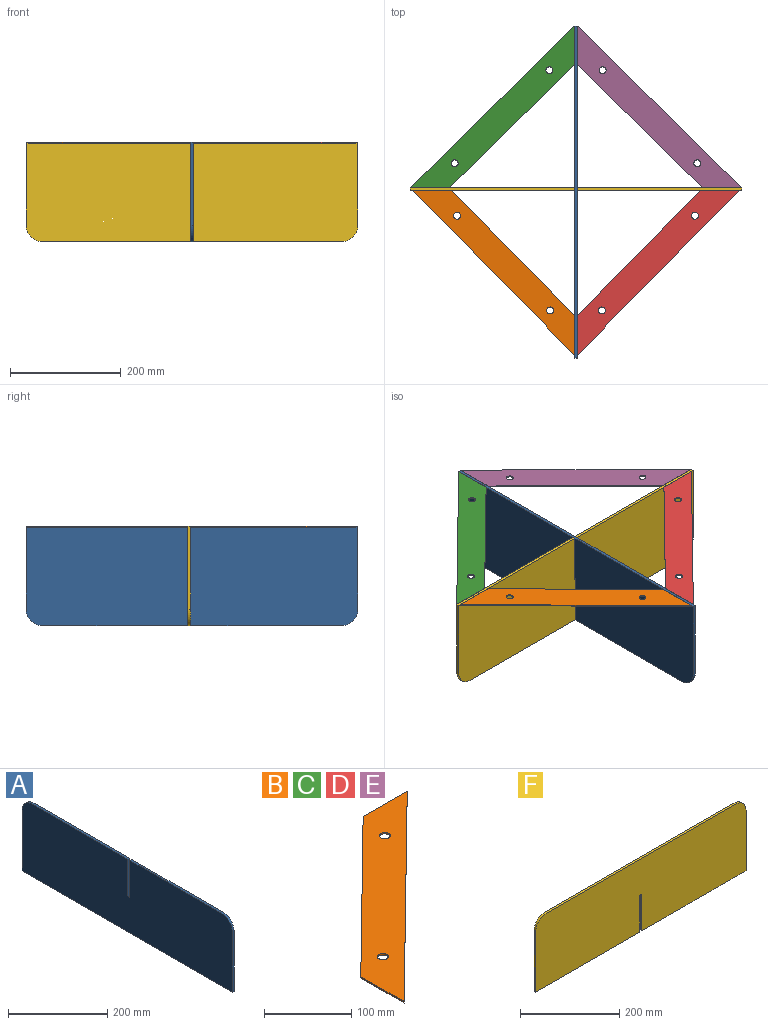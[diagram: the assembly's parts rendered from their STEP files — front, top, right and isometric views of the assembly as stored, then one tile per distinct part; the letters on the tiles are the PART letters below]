
ASSEMBLY  parts=6 mates=9
PART A: 12 faces, bbox 5x600x180 mm
  f0: plane 91x5mm, normal (0,1,0), area 455mm2, adj f1,f7,f8,f9
  f1: plane 262x5mm, normal (0,0,1), area 1310mm2, adj f0,f8,f9,f10
  f2: plane 150x5mm, normal (0,-1,0), area 750mm2, adj f3,f8,f9,f10
  f3: plane 600x5mm, normal (0,0,-1), area 3000mm2, adj f2,f4,f8,f9
  f4: plane 150x5mm, normal (0,1,0), area 750mm2, adj f3,f8,f9,f11
  f5: plane 272x5mm, normal (0,0,1), area 1360mm2, adj f6,f8,f9,f11
  f6: plane 91x5mm, normal (0,-1,0), area 455mm2, adj f5,f7,f8,f9
  f7: plane 6x5mm, normal (0,0,1), area 30mm2, adj f0,f6,f8,f9
  f8: plane 600x180mm, normal (1,0,0), area 107067.7mm2, adj f0,f1,f2,f3,f4,f5,f6,f7
  f9: plane 600x180mm, normal (-1,0,0), area 107067.7mm2, adj f0,f1,f2,f3,f4,f5,f6,f7
  f10: cylinder r=30mm len=30mm, axis (-1,0,0), area 235.6mm2, adj f1,f2,f8,f9
  f11: cylinder r=30mm len=30mm, axis (1,0,0), area 235.6mm2, adj f4,f5,f8,f9
PART B: 8 faces, bbox 297.5x292.5x2 mm
  f0: plane 70.12x2mm, normal (-1,0,0), area 140.2mm2, adj f1,f3,f4,f5
  f1: plane 226.18x222.38mm, normal (-0.7,0.71,0), area 634.4mm2, adj f0,f2,f4,f5
  f2: plane 71.32x2mm, normal (0,1,0), area 142.6mm2, adj f1,f3,f4,f5
  f3: plane 297.5x292.5mm, normal (0.7,-0.71,0), area 834.4mm2, adj f0,f2,f4,f5
  f4: plane 297.5x292.5mm, normal (0,0,1), area 18114.6mm2, adj f0,f1,f2,f3,f6,f7
  f5: plane 297.5x292.5mm, normal (0,0,-1), area 18114.6mm2, adj f0,f1,f2,f3,f6,f7
  f6: cylinder r=6.25mm len=12.5mm, axis (0,0,-1), area 78.5mm2, adj f4,f5
  f7: cylinder r=6.25mm len=12.5mm, axis (0,0,-1), area 78.5mm2, adj f4,f5
PART C: same geometry as B
PART D: same geometry as B
PART E: same geometry as B
PART F: 12 faces, bbox 600x5x180 mm
  f0: plane 91x5mm, normal (-1,0,0), area 455mm2, adj f1,f7,f8,f9
  f1: plane 297x5mm, normal (0,0,-1), area 1485mm2, adj f0,f2,f8,f9
  f2: plane 150x5mm, normal (1,0,0), area 750mm2, adj f1,f8,f9,f10
  f3: plane 540x5mm, normal (0,0,1), area 2700mm2, adj f8,f9,f10,f11
  f4: plane 150x5mm, normal (-1,0,0), area 750mm2, adj f5,f8,f9,f11
  f5: plane 297x5mm, normal (0,0,-1), area 1485mm2, adj f4,f6,f8,f9
  f6: plane 91x5mm, normal (1,0,0), area 455mm2, adj f5,f7,f8,f9
  f7: plane 6x5mm, normal (0,0,-1), area 30mm2, adj f0,f6,f8,f9
  f8: plane 600x180mm, normal (0,-1,0), area 107067.7mm2, adj f0,f1,f2,f3,f4,f5,f6,f7
  f9: plane 600x180mm, normal (0,1,0), area 107067.7mm2, adj f0,f1,f2,f3,f4,f5,f6,f7
  f10: cylinder r=30mm len=30mm, axis (0,-1,0), area 235.6mm2, adj f2,f3,f8,f9
  f11: cylinder r=30mm len=30mm, axis (0,1,0), area 235.6mm2, adj f3,f4,f8,f9
PLACE A rot(axis=(1,0,0),180deg) t=(0,5.03,90.47)mm
PLACE B rot(axis=(0,0,-1),90deg) t=(2.5,7.53,88.47)mm
PLACE C rot(axis=(0,0,1),180deg) t=(0,5.03,88.47)mm
PLACE D rot(axis=(0.71,-0.71,0),180deg) t=(-2.5,7.53,90.47)mm
PLACE E rot(axis=(1,0,0),180deg) t=(0,5.03,90.47)mm
PLACE F rot(axis=(1,0,0),180deg) t=(0,5.03,90.47)mm
MATE planar D.f5 <-> F.f1  axis (0,0,1) through (132.03,-126.71,90.47)mm
MATE planar C.f4 <-> A.f3  axis (0,0,1) through (-134.24,139.56,90.47)mm
MATE planar D.f2 <-> A.f8  axis (-1,0,0) through (2.5,-256.82,89.47)mm
MATE planar D.f0 <-> F.f9  axis (0,1,0) through (259.94,5.03,89.47)mm
MATE planar B.f2 <-> A.f9  axis (1,0,0) through (-2.5,-256.82,89.47)mm
MATE planar B.f4 <-> A.f3  axis (0,0,1) through (-132.03,-126.71,90.47)mm
MATE planar C.f2 <-> F.f8  axis (0,-1,0) through (-264.34,10.03,89.47)mm
MATE planar C.f0 <-> A.f9  axis (1,0,0) through (-2.5,267.47,89.47)mm
MATE planar B.f0 <-> F.f9  axis (0,1,0) through (-259.94,5.03,89.47)mm
